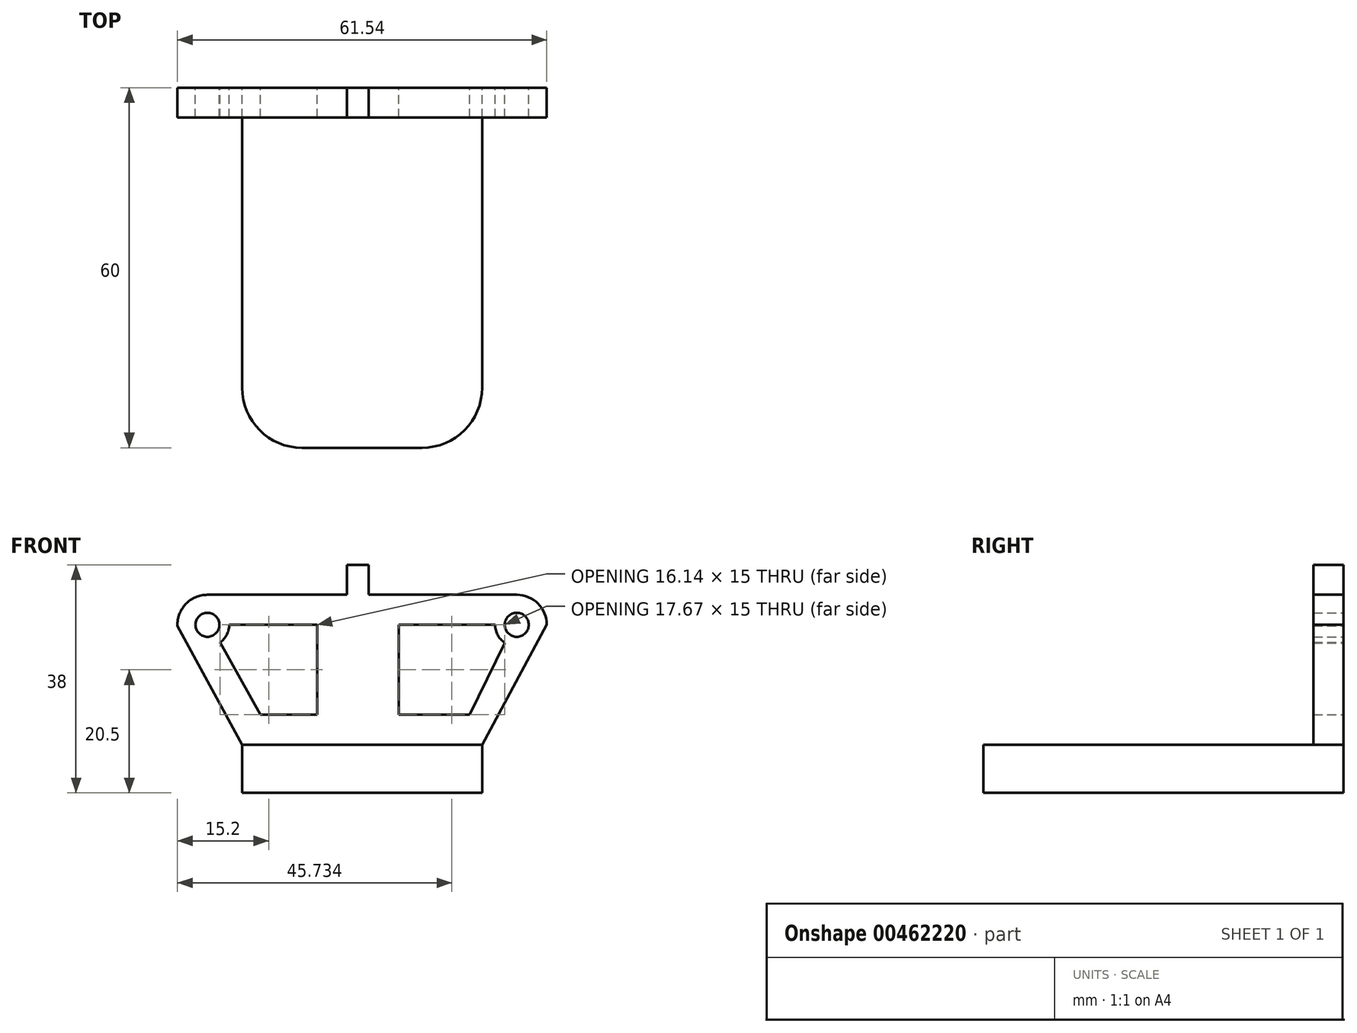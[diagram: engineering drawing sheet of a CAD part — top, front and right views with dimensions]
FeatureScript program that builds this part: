
annotation { "Feature Type Name" : "Feature", "Feature Type Description" : "" }
export const myFeature = defineFeature(function(context is Context, id is Id, definition is map)
    precondition{}
    {
        {
            var Q0;
            Q0=qCreatedBy(makeId("Front.planeOp"),FACE);
            var sketch = newSketch(context, id + "F0", { "sketchPlane" : qUnion([Q0])});
            skLineSegment(sketch, "E0", {"start": v(-20, 0) * mm, "end": v(-20, -8) * mm});
            skLineSegment(sketch, "E1", {"start": v(-20, -8) * mm, "end": v(20, -8) * mm});
            skLineSegment(sketch, "E2", {"start": v(20, -8) * mm, "end": v(20, 0) * mm});
            skLineSegment(sketch, "E3", {"start": v(-20, 0) * mm, "end": v(20, 0) * mm});
            skCircle(sketch, "E4", {"center": v(-25.77, 20) * mm, "radius": 2 * mm});
            skCircle(sketch, "E5", {"center": v(25.77, 20) * mm, "radius": 2 * mm});
            skLineSegment(sketch, "E6", {"start": v(-20, 0) * mm, "end": v(-30.77, 19.84) * mm});
            skArc(sketch, "E7", {"start": v(-30.77, 19.84) * mm, "mid": v(-29.36, 23.48) * mm, "end": v(-25.77, 25) * mm});
            skArc(sketch, "E8", {"start": v(30.77, 20) * mm, "mid": v(29.3, 23.54) * mm, "end": v(25.77, 25) * mm});
            skLineSegment(sketch, "E9", {"start": v(-25.77, 25) * mm, "end": v(25.77, 25) * mm});
            skLineSegment(sketch, "E10", {"start": v(30.77, 20) * mm, "end": v(20, 0) * mm});
            skLineSegment(sketch, "E11", {"start": v(-22.14, 20) * mm, "end": v(-7.5, 20) * mm});
            skLineSegment(sketch, "E12", {"start": v(-7.5, 5) * mm, "end": v(-7.5, 20) * mm});
            skLineSegment(sketch, "E13", {"start": v(-2.5, 20) * mm, "end": v(-2.5, 5) * mm});
            skLineSegment(sketch, "E14", {"start": v(1.13, 20) * mm, "end": v(1.13, 5) * mm});
            skLineSegment(sketch, "E15", {"start": v(6.13, 20) * mm, "end": v(6.13, 5) * mm});
            skArc(sketch, "E16", {"start": v(-22.14, 20) * mm, "mid": v(-22.54, 18.35) * mm, "end": v(-23.64, 17.06) * mm});
            skArc(sketch, "E17", {"start": v(22.17, 20) * mm, "mid": v(22.6, 18.29) * mm, "end": v(23.8, 17) * mm});
            skLineSegment(sketch, "E18", {"start": v(-23.64, 17.06) * mm, "end": v(-16.91, 5) * mm});
            skLineSegment(sketch, "E19", {"start": v(-16.91, 5) * mm, "end": v(-7.5, 5) * mm});
            skLineSegment(sketch, "E20", {"start": v(17.9, 5) * mm, "end": v(23.8, 17) * mm});
            skLineSegment(sketch, "E21.trimOffspring", {"start": v(-2.5, 20) * mm, "end": v(1.13, 20) * mm});
            skLineSegment(sketch, "E22.trimOffspring", {"start": v(6.13, 20) * mm, "end": v(22.17, 20) * mm});
            skLineSegment(sketch, "E23.trimOffspring", {"start": v(6.13, 5) * mm, "end": v(17.9, 5) * mm});
            skLineSegment(sketch, "E24.trimOffspring", {"start": v(-2.5, 5) * mm, "end": v(1.13, 5) * mm});
            skSolve(sketch);
        }
        {
            var Q0;
            Q0=makeQuery(id+"F0.imprint","IMPRINT",FACE,{"disambiguationData":[TD([[makeQuery(id+"F0.imprint","IMPRINT",EDGE,{"derivedFrom":sQuery(id+"F0.wireOp",EDGE,"E0")}),1.0]])]});
            extrude(context, id + "F1", {"entities" : qUnion([Q0]), "depth" : 60 * mm});
        }
        {
            var Q0;
            Q0 = qSketchRegion(id + "F0", true);
            var Q1;
            Q1=makeQuery(id+"F1.opExtrude","CAP_FACE",FACE,{"disambiguationData":[OSD([sQuery(id+"F0.wireOp",EDGE,"E0"),sQuery(id+"F0.wireOp",EDGE,"E1"),sQuery(id+"F0.wireOp",EDGE,"E2"),sQuery(id+"F0.wireOp",EDGE,"E3")])],"isStart":true});
            extrude(context, id + "F2", {"entities" : qUnion([Q0, Q1]), "operationType" : NewBodyOperationType.ADD, "depth" : 5 * mm});
        }
        {
            var Q0;
            Q0=makeQuery(id+"F1.opExtrude","CAP_EDGE",EDGE,{"disambiguationData":[OSD([sQuery(id+"F0.wireOp",EDGE,"E0")])],"isStart":false});
            fillet(context, id + "F3", {"entities" : qUnion([Q0]), "radius" : 10 * mm, "tangentPropagation" : true, "allowEdgeOverflow" : false});
        }
        {
            var Q0;
            Q0=makeQuery(id+"F1.opExtrude","CAP_EDGE",EDGE,{"disambiguationData":[OSD([sQuery(id+"F0.wireOp",EDGE,"E2")])],"isStart":false});
            fillet(context, id + "F4", {"entities" : qUnion([Q0]), "radius" : 10 * mm, "tangentPropagation" : true, "allowEdgeOverflow" : false});
        }
        {
            var Q0;
            Q0=makeQuery(id+"F2.opExtrude","SWEPT_FACE",FACE,{"disambiguationData":[OSD([sQuery(id+"F0.wireOp",EDGE,"E24.trimOffspring")])]});
            extrude(context, id + "F5", {"entities" : qUnion([Q0]), "operationType" : NewBodyOperationType.ADD, "depth" : 25 * mm});
        }
    });
